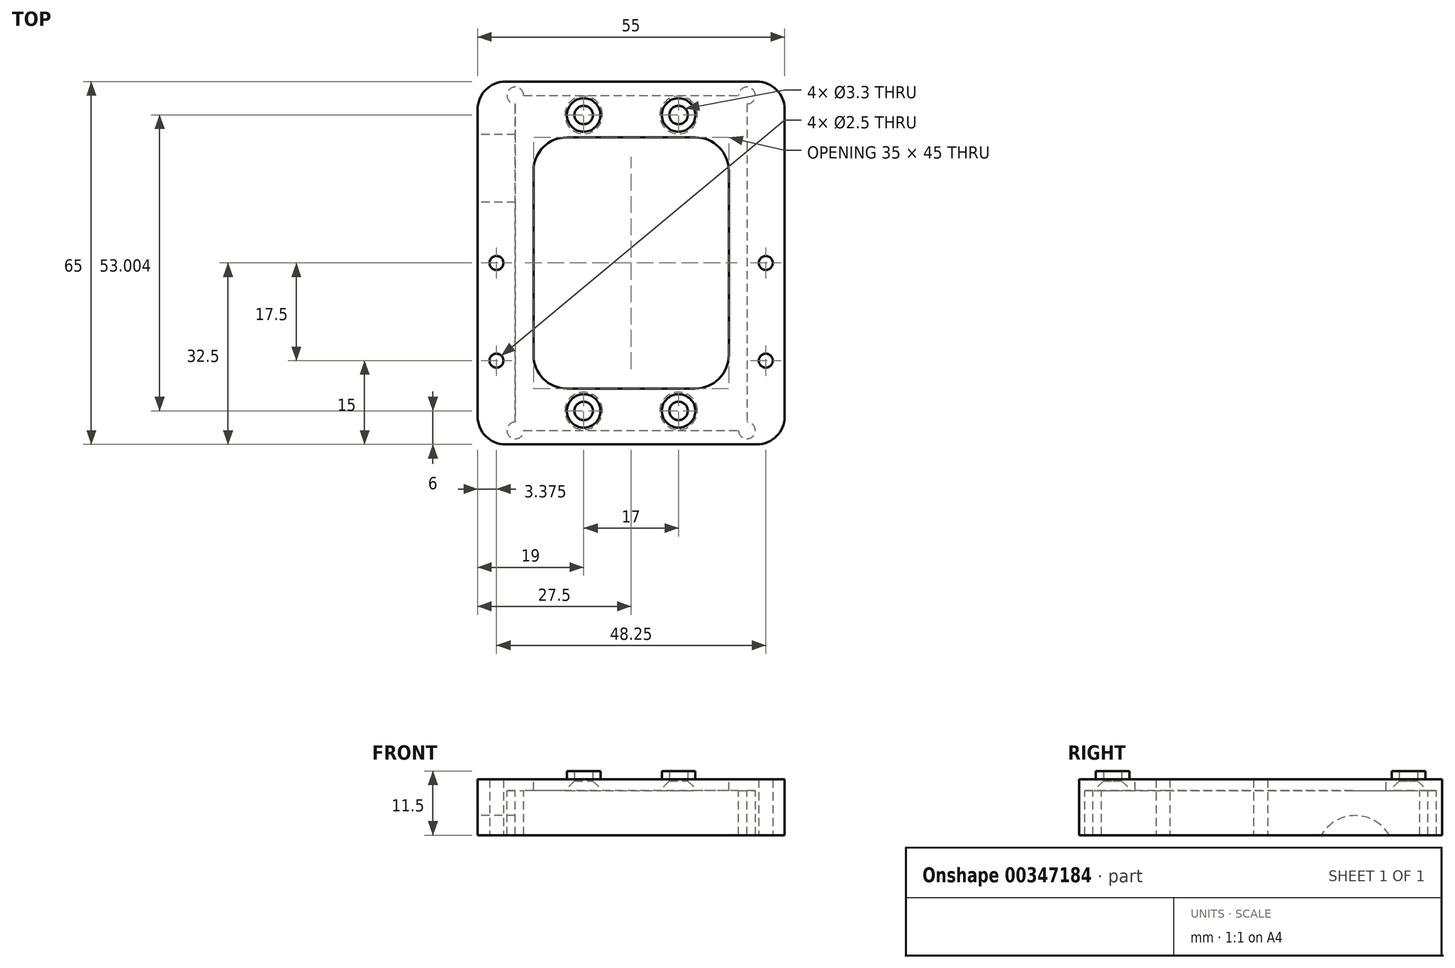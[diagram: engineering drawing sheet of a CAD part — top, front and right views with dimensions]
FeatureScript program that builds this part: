
annotation { "Feature Type Name" : "Feature", "Feature Type Description" : "" }
export const myFeature = defineFeature(function(context is Context, id is Id, definition is map)
    precondition{}
    {
        {
            var Q0;
            Q0=qCreatedBy(makeId("Front.planeOp"),FACE);
            var sketch = newSketch(context, id + "F0", { "sketchPlane" : qUnion([Q0])});
            skLineSegment(sketch, "E0.bottom", {"start": v(27.5, -5) * mm, "end": v(-27.5, -5) * mm});
            skLineSegment(sketch, "E0.top", {"start": v(27.5, 5) * mm, "end": v(-27.5, 5) * mm});
            skLineSegment(sketch, "E0.left", {"start": v(27.5, -5) * mm, "end": v(27.5, 5) * mm});
            skLineSegment(sketch, "E0.right", {"start": v(-27.5, -5) * mm, "end": v(-27.5, 5) * mm});
            skPoint(sketch, "E0.middle", {"position": v(0, 0) * mm});
            skSolve(sketch);
        }
        {
            var Q0;
            Q0=qSketchRegion(id+"F0",true);
            extrude(context, id + "F1", {"entities" : qUnion([Q0]), "endBound" : BoundingType.SYMMETRIC, "depth" : 65 * mm});
        }
        {
            var Q0;
            Q0=qCreatedBy(makeId("Top.planeOp"),FACE);
            var sketch = newSketch(context, id + "F2", { "sketchPlane" : qUnion([Q0])});
            skLineSegment(sketch, "E1.bottom", {"start": v(11.5, -22.5) * mm, "end": v(-11.5, -22.5) * mm});
            skLineSegment(sketch, "E1.top", {"start": v(11.5, 22.5) * mm, "end": v(-11.5, 22.5) * mm});
            skLineSegment(sketch, "E1.left", {"start": v(17.5, -16.5) * mm, "end": v(17.5, 16.5) * mm});
            skLineSegment(sketch, "E1.right", {"start": v(-17.5, -16.5) * mm, "end": v(-17.5, 16.5) * mm});
            skPoint(sketch, "E1.middle", {"position": v(0, 0) * mm});
            skPoint(sketch, "E2.visualSharp", {"position": v(17.5, 22.5) * mm});
            skArc(sketch, "E2.filletArc", {"start": v(17.5, 16.5) * mm, "mid": v(15.74, 20.74) * mm, "end": v(11.5, 22.5) * mm});
            skPoint(sketch, "E3.visualSharp", {"position": v(17.5, -22.5) * mm});
            skArc(sketch, "E3.filletArc", {"start": v(11.5, -22.5) * mm, "mid": v(15.74, -20.74) * mm, "end": v(17.5, -16.5) * mm});
            skPoint(sketch, "E4.visualSharp", {"position": v(-17.5, 22.5) * mm});
            skArc(sketch, "E4.filletArc", {"start": v(-11.5, 22.5) * mm, "mid": v(-15.74, 20.74) * mm, "end": v(-17.5, 16.5) * mm});
            skPoint(sketch, "E5.visualSharp", {"position": v(-17.5, -22.5) * mm});
            skArc(sketch, "E5.filletArc", {"start": v(-17.5, -16.5) * mm, "mid": v(-15.74, -20.74) * mm, "end": v(-11.5, -22.5) * mm});
            skSolve(sketch);
        }
        {
            var Q0;
            Q0=makeQuery(id+"F1.opExtrude","CAP_EDGE",EDGE,{"disambiguationData":[OSD([sQuery(id+"F0.wireOp",EDGE,"E0.left")])],"isStart":false});
            var Q1;
            Q1=makeQuery(id+"F1.opExtrude","CAP_EDGE",EDGE,{"disambiguationData":[OSD([sQuery(id+"F0.wireOp",EDGE,"E0.right")])],"isStart":false});
            var Q2;
            Q2=makeQuery(id+"F1.opExtrude","CAP_EDGE",EDGE,{"disambiguationData":[OSD([sQuery(id+"F0.wireOp",EDGE,"E0.right")])],"isStart":true});
            var Q3;
            Q3=makeQuery(id+"F1.opExtrude","CAP_EDGE",EDGE,{"disambiguationData":[OSD([sQuery(id+"F0.wireOp",EDGE,"E0.left")])],"isStart":true});
            fillet(context, id + "F3", {"entities" : qUnion([Q0, Q1, Q2, Q3]), "radius" : 5 * mm, "tangentPropagation" : true, "allowEdgeOverflow" : false});
        }
        {
            var Q0;
            Q0=qSketchRegion(id+"F2",true);
            var Q1;
            Q1=makeQuery(id+"F1.opExtrude","SWEPT_FACE",FACE,{"disambiguationData":[OSD([sQuery(id+"F0.wireOp",EDGE,"E0.top")])]});
            extrude(context, id + "F4", {"entities" : qUnion([Q0]), "operationType" : NewBodyOperationType.REMOVE, "endBound" : BoundingType.SYMMETRIC, "oppositeDirection" : true, "endBoundEntityFace" : qUnion([Q1]), "depth" : 25 * mm});
        }
        {
            var Q0;
            Q0=qCreatedBy(makeId("Top.planeOp"),FACE);
            var sketch = newSketch(context, id + "F5", { "sketchPlane" : qUnion([Q0])});
            skLineSegment(sketch, "E6.bottom", {"start": v(20.75, -30) * mm, "end": v(-20.75, -30) * mm});
            skLineSegment(sketch, "E6.top", {"start": v(20.75, 30) * mm, "end": v(-20.75, 30) * mm});
            skLineSegment(sketch, "E6.left", {"start": v(20.75, -30) * mm, "end": v(20.75, 30) * mm});
            skLineSegment(sketch, "E6.right", {"start": v(-20.75, -30) * mm, "end": v(-20.75, 30) * mm});
            skPoint(sketch, "E6.middle", {"position": v(0, 0) * mm});
            skCircle(sketch, "E7", {"center": v(-20.75, 30) * mm, "radius": 1.5 * mm});
            skCircle(sketch, "E8", {"center": v(20.75, 30) * mm, "radius": 1.5 * mm});
            skCircle(sketch, "E9", {"center": v(-20.75, -30) * mm, "radius": 1.5 * mm});
            skCircle(sketch, "E10", {"center": v(20.75, -30) * mm, "radius": 1.5 * mm});
            skSolve(sketch);
        }
        {
            var Q0;
            Q0=qSketchRegion(id+"F5",true);
            extrude(context, id + "F6", {"entities" : qUnion([Q0]), "operationType" : NewBodyOperationType.REMOVE, "oppositeDirection" : true, "depth" : 30 * mm});
        }
        {
            var Q0;
            Q0=qSketchRegion(id+"F5",true);
            extrude(context, id + "F7", {"entities" : qUnion([Q0]), "operationType" : NewBodyOperationType.REMOVE, "depth" : 3 * mm});
        }
        {
            var Q0;
            Q0=makeQuery(id+"F7.boolean.opBoolean","COPY",FACE,{"derivedFrom":makeQuery(id+"F7.opExtrude","CAP_FACE",FACE,{"disambiguationData":[OSD([sQuery(id+"F5.wireOp",EDGE,"E6.bottom"),sQuery(id+"F5.wireOp",EDGE,"E6.top"),sQuery(id+"F5.wireOp",EDGE,"E6.left"),sQuery(id+"F5.wireOp",EDGE,"E6.right"),sQuery(id+"F5.wireOp",EDGE,"E7"),sQuery(id+"F5.wireOp",EDGE,"E8"),sQuery(id+"F5.wireOp",EDGE,"E9"),sQuery(id+"F5.wireOp",EDGE,"E10")])],"isStart":false})});
            var sketch = newSketch(context, id + "F8", { "sketchPlane" : qUnion([Q0])});
            skPoint(sketch, "E11", {"position": v(-8.5, -26.5) * mm});
            skPoint(sketch, "E12", {"position": v(8.5, -26.5) * mm});
            skPoint(sketch, "E13", {"position": v(8.5, 26.5) * mm});
            skPoint(sketch, "E14", {"position": v(-8.5, 26.5) * mm});
            skSolve(sketch);
        }
        {
            var Q0;
            Q0=sQuery(id+"F8.wireOp",VERTEX,"E11");
            var Q1;
            Q1=sQuery(id+"F8.wireOp",VERTEX,"E12");
            var Q2;
            Q2=makeQuery(id+"F1.opExtrude","SWEPT_BODY",BODY,{"disambiguationData":[OSD([sQuery(id+"F0.wireOp",EDGE,"E0.bottom"),sQuery(id+"F0.wireOp",EDGE,"E0.top"),sQuery(id+"F0.wireOp",EDGE,"E0.left"),sQuery(id+"F0.wireOp",EDGE,"E0.right")])]});
            hole(context, id + "F9", {"style" : HoleStyle.C_SINK, "endStyle" : HoleEndStyle.THROUGH, "standardTappedOrClearance" : lookupTablePath({ "standard" : "ISO", "fit" : "Normal", "size" : "M3", "type" : "Clearance" }), "standardBlindInLast" : lookupTablePath({ "fit" : "Standard", "standard" : "ISO", "size" : "M3", "type" : "Clearance" }), "holeDiameter" : 3.3 * mm, "cSinkDiameter" : 6.72 * mm, "cSinkAngle" : 90 * degree, "tappedDepth" : 12 * mm, "tapClearance" : 3, "locations" : qUnion([Q0, Q1]), "scope" : qUnion([Q2])});
        }
        {
            var Q0;
            Q0=makeQuery(id+"F1.opExtrude","SWEPT_FACE",FACE,{"disambiguationData":[OSD([sQuery(id+"F0.wireOp",EDGE,"E0.top")])]});
            var sketch = newSketch(context, id + "F10", { "sketchPlane" : qUnion([Q0])});
            skCircle(sketch, "E15", {"center": v(8.5, 26.5) * mm, "radius": 3 * mm});
            skCircle(sketch, "E16", {"center": v(-8.5, 26.5) * mm, "radius": 3 * mm});
            skCircle(sketch, "E17", {"center": v(-8.5, -26.5) * mm, "radius": 3 * mm});
            skCircle(sketch, "E18", {"center": v(8.5, -26.5) * mm, "radius": 3 * mm});
            skSolve(sketch);
        }
        {
            var Q0;
            Q0=qSketchRegion(id+"F10",true);
            extrude(context, id + "F11", {"entities" : qUnion([Q0]), "operationType" : NewBodyOperationType.ADD, "depth" : 1.5 * mm});
        }
        {
            var Q0;
            Q0=sQuery(id+"F8.wireOp",VERTEX,"E11");
            var Q1;
            Q1=sQuery(id+"F8.wireOp",VERTEX,"E12");
            var Q2;
            Q2=sQuery(id+"F8.wireOp",VERTEX,"E13");
            var Q3;
            Q3=sQuery(id+"F8.wireOp",VERTEX,"E14");
            var Q4;
            Q4=makeQuery(id+"F1.opExtrude","SWEPT_BODY",BODY,{"disambiguationData":[OSD([sQuery(id+"F0.wireOp",EDGE,"E0.bottom"),sQuery(id+"F0.wireOp",EDGE,"E0.top"),sQuery(id+"F0.wireOp",EDGE,"E0.left"),sQuery(id+"F0.wireOp",EDGE,"E0.right")])]});
            hole(context, id + "F12", {"style" : HoleStyle.C_SINK, "endStyle" : HoleEndStyle.BLIND, "standardTappedOrClearance" : lookupTablePath({ "standard" : "ISO", "fit" : "Normal", "size" : "M3", "type" : "Clearance" }), "standardBlindInLast" : lookupTablePath({ "fit" : "Standard", "standard" : "ISO", "size" : "M3", "type" : "Clearance" }), "holeDiameter" : 3.3 * mm, "cSinkDiameter" : 6.72 * mm, "cSinkAngle" : 90 * degree, "holeDepth" : 13.5 * mm, "tappedDepth" : 12 * mm, "tapClearance" : 3, "locations" : qUnion([Q0, Q1, Q2, Q3]), "scope" : qUnion([Q4])});
        }
        {
            var Q0;
            Q0=makeQuery(id+"F1.opExtrude","SWEPT_FACE",FACE,{"disambiguationData":[OSD([sQuery(id+"F0.wireOp",EDGE,"E0.bottom")])]});
            var sketch = newSketch(context, id + "F13", { "sketchPlane" : qUnion([Q0])});
            skPoint(sketch, "E19", {"position": v(-24.12, 0) * mm});
            skPoint(sketch, "E20", {"position": v(24.12, 0) * mm});
            skPoint(sketch, "E21", {"position": v(-24.12, 17.5) * mm});
            skPoint(sketch, "E22", {"position": v(24.12, 17.5) * mm});
            skSolve(sketch);
        }
        {
            var Q0;
            Q0=sQuery(id+"F13.wireOp",VERTEX,"E19");
            var Q1;
            Q1=sQuery(id+"F13.wireOp",VERTEX,"E20");
            var Q2;
            Q2=sQuery(id+"F13.wireOp",VERTEX,"E21");
            var Q3;
            Q3=sQuery(id+"F13.wireOp",VERTEX,"E22");
            var Q4;
            Q4=makeQuery(id+"F1.opExtrude","SWEPT_BODY",BODY,{"disambiguationData":[OSD([sQuery(id+"F0.wireOp",EDGE,"E0.bottom"),sQuery(id+"F0.wireOp",EDGE,"E0.top"),sQuery(id+"F0.wireOp",EDGE,"E0.left"),sQuery(id+"F0.wireOp",EDGE,"E0.right")])]});
            hole(context, id + "F14", {"style" : HoleStyle.SIMPLE, "endStyle" : HoleEndStyle.BLIND, "standardTappedOrClearance" : lookupTablePath({ "standard" : "ISO", "engagement" : "75%", "pitch" : "0.5 mm", "size" : "M3", "type" : "Tapped" }), "standardBlindInLast" : lookupTablePath({ "standard" : "ISO", "engagement" : "75%", "pitch" : "0.5 mm", "size" : "M3", "type" : "Tapped" }), "holeDiameter" : 2.5 * mm, "showTappedDepth" : true, "holeDepth" : 13.5 * mm, "tappedDepth" : 12 * mm, "tapClearance" : 3, "locations" : qUnion([Q0, Q1, Q2, Q3]), "scope" : qUnion([Q4]), "majorDiameter" : 3 * mm});
        }
        {
            var Q0;
            Q0=makeQuery(id+"F1.opExtrude","SWEPT_FACE",FACE,{"disambiguationData":[OSD([sQuery(id+"F0.wireOp",EDGE,"E0.right")])]});
            var sketch = newSketch(context, id + "F15", { "sketchPlane" : qUnion([Q0])});
            skPoint(sketch, "E23", {"position": v(-16.97, -8.5) * mm});
            skCircle(sketch, "E24", {"center": v(-16.97, -8.5) * mm, "radius": 7 * mm});
            skSolve(sketch);
        }
        {
            var Q0;
            {var subQ0=sQuery(id+"F15.wireOp",EDGE,"E24");var subQ1=makeQuery(id+"F1.opExtrude","SWEPT_EDGE",EDGE,{"disambiguationData":[OSD([sQuery(id+"F0.wireOp",EDGE,"E0.bottom"),sQuery(id+"F0.wireOp",EDGE,"E0.right")])]});var subQ2=makeQuery(id+"F15.imprint","INTERSECT",VERTEX,{"disambiguationData":[OD(0.0)],"derivedFrom":[subQ1,subQ0]});Q0=makeQuery(id+"F15.imprint","IMPRINT",FACE,{"disambiguationData":[TD([[makeQuery(id+"F15.imprint","IMPRINT",EDGE,{"disambiguationData":[TD([[subQ2,1.0]])],"derivedFrom":subQ0}),1.0]])]});}
            extrude(context, id + "F16", {"entities" : qUnion([Q0]), "operationType" : NewBodyOperationType.REMOVE, "oppositeDirection" : true, "depth" : 12 * mm});
        }
    });
